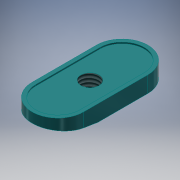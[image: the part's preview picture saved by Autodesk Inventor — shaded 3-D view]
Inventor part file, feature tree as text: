
AUTODESK INVENTOR PART (.ipt)
format: ipt  version: 2018 (Build 220112000, 112)  size: 176,128 bytes
history: native  units: in
note: dims shown in document units (in); Inventor stores cm internally (conversion verified against a paired STEP export)
features: sketch x6, extrude x4, hole x1, thread x1, plane x1, revolve x1
ambient origin geometry x8: Origin, YZ Plane, XZ Plane, XY Plane, X Axis, Y Axis, Z Axis, Center Point
bodies: Solid1 (feature_tree)
feature tree (14):
  extrude  "Extrusion1"  Depth=0.02in TaperAngle=0.0deg
  extrude  "Extrusion2"  Depth=0.25in TaperAngle=0.0deg
  hole  "Hole1"  [1 undecoded]
  thread  "Thread1"  [1 undecoded]
  extrude  "Extrusion3"  Depth=0.18in
  plane  "Work Plane1"
  revolve  "Revolution1"  [1 undecoded]
  extrude  "Extrusion4"  Depth=0.05in
  sketch  "Sketch1"  dims[d3=0.22in d4=0.0in d8=0.02in d9=0.0in]
  sketch  "Sketch2"  dims[d10=0.25in]
  sketch  "Sketch3"  dims[d11=0.25in d12=0.75in d13=0.375in d14=0.25in d15=0.5635in d16=1.0in d17=0.8108in d18=1.0in d19=0.0in]
  sketch  "Sketch4"  dims[d20=0.02in d21=0.0in d22=0.1in d23=0.5in]
  sketch  "Sketch5"  dims[d24=90.0deg d25=0.18in]
  sketch  "Sketch6"  dims[d26=0.4375in d27=0.05in d28=0.0in d29=0.0618in d30=0.24in d31=0.54in d32=0.05in d33=0.05in d34=0.05in d36=0.875in d37=0.875in d38=0.875in]
note: 3 required parameter values undecoded (feature->parameter linkage not recoverable at this tier; creation-order binding heuristic only, values carry confidence <= 0.55)